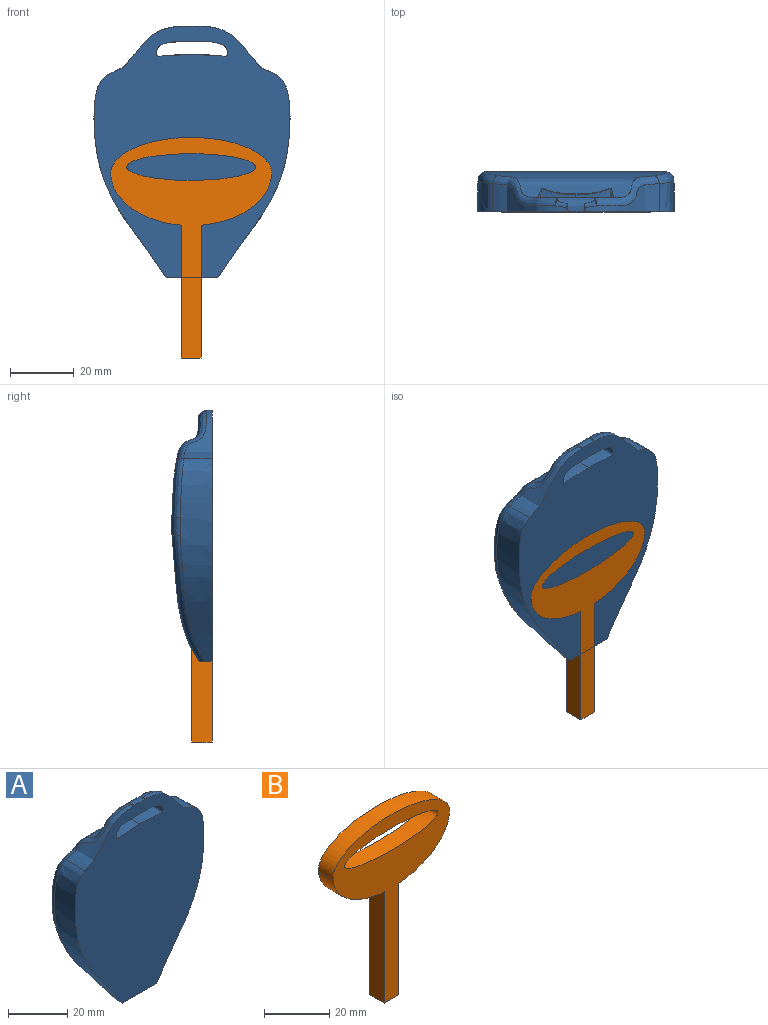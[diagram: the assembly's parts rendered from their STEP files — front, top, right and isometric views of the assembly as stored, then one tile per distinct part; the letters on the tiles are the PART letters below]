
ASSEMBLY  parts=2 mates=1
PART A: 34 faces, bbox 62.2x13.4x80.2 mm
  f0: bspline ~1.98x0.93mm, area 0.2mm2, adj f9,f10,f11
  f1: extruded ~54.94x39.8mm, area 1494.4mm2, adj f3,f4,f5,f6,f7,f13
  f2: bspline ~1.98x0.93mm, area 0.2mm2, adj f15,f16,f17
  f3: bspline ~10.82x3.82mm, area 23.1mm2, adj f1,f4,f13,f14,f27
  f4: bspline ~43.26x24.45mm, area 173.7mm2, adj f1,f3,f5,f26,f27
  f5: plane 15.96x1.26mm, normal (0,0.02,-1), area 12.5mm2, adj f1,f4,f6,f26
  f6: bspline ~43.26x24.45mm, area 173.8mm2, adj f1,f5,f7,f25,f26
  f7: bspline ~11.83x4.04mm, area 23.1mm2, adj f1,f6,f12,f13,f25
  f8: bspline ~1.1x0.26mm, area 0.1mm2, adj f9,f21,f24
  f9: bspline ~4.26x2.61mm, area 5.6mm2, adj f0,f8,f21,f24,f29
  f10: bspline ~1.25x0.54mm, area 0.1mm2, adj f0,f11,f24
  f11: bspline ~20.97x16.97mm, area 94.1mm2, adj f0,f10,f12,f24,f29
  f12: bspline ~19.64x6.21mm, area 75.1mm2, adj f7,f11,f13,f24,f25,f29
  f13: plane 56.13x5.66mm, normal (0,1,0), area 314.2mm2, adj f1,f3,f7,f12,f14,f24
  f14: bspline ~19.61x6.15mm, area 75.1mm2, adj f3,f13,f15,f24,f27,f28
  f15: bspline ~20.97x16.97mm, area 94.1mm2, adj f2,f14,f16,f24,f28
  f16: bspline ~1.25x0.54mm, area 0.1mm2, adj f2,f15,f24
  f17: bspline ~4.01x2.57mm, area 5.6mm2, adj f2,f18,f20,f24,f28
  f18: bspline ~1.1x0.27mm, area 0.1mm2, adj f17,f20,f24
  f19: bspline ~18.08x5.39mm, area 14.5mm2, adj f24,f30,f32
  f20: bspline ~0.22x0.19mm, area 0mm2, adj f17,f18,f22
  f21: bspline ~0.22x0.19mm, area 0mm2, adj f8,f9,f23
  f22: bspline ~1.69x0.72mm, area 0.3mm2, adj f20,f24,f28,f33
  f23: bspline ~1.69x0.72mm, area 0.3mm2, adj f21,f24,f29,f33
  f24: extruded ~56.41x33.39mm, area 1410.5mm2, adj f8,f9,f10,f11,f12,f13,f14,f15
  f25: extruded ~63.73x22.62mm, area 596.7mm2, adj f6,f7,f12,f26,f29,f33
  f26: plane 16.35x3.32mm, normal (0,0,-1), area 52.1mm2, adj f4,f5,f6,f25,f27,f33
  f27: extruded ~63.73x22.62mm, area 596.7mm2, adj f3,f4,f14,f26,f28,f33
  f28: extruded ~23.59x15.13mm, area 115.1mm2, adj f14,f15,f17,f22,f27,f33
  f29: extruded ~23.59x15.13mm, area 115.1mm2, adj f9,f11,f12,f23,f25,f33
  f30: bspline ~18.08x5.39mm, area 14.5mm2, adj f19,f24,f31
  f31: extruded ~11.21x7.24mm, area 119.8mm2, adj f30,f32,f33
  f32: extruded ~11.21x7.24mm, area 119.8mm2, adj f19,f31,f33
  f33: plane 78.9x61.81mm, normal (0,-1,0), area 3529.4mm2, adj f22,f23,f24,f25,f26,f27,f28,f29
PART B: 9 faces, bbox 50.5x6.4x69.2 mm
  f0: plane 41.66x6.35mm, normal (1,0,0), area 264.6mm2, adj f1,f6,f7,f8
  f1: extruded ~22.08x15.45mm, area 184.9mm2, adj f0,f2,f7,f8
  f2: extruded ~50.46x12.08mm, area 388mm2, adj f1,f3,f7,f8
  f3: extruded ~22.08x15.45mm, area 184.9mm2, adj f2,f4,f7,f8
  f4: plane 41.66x6.35mm, normal (-1,0,0), area 264.6mm2, adj f3,f6,f7,f8
  f5: extruded ~40.38x8.43mm, area 541.2mm2, adj f7,f8
  f6: plane 6.35x6.19mm, normal (0,0,-1), area 39.3mm2, adj f0,f4,f7,f8
  f7: plane 69.19x50.48mm, normal (0,-1,0), area 1085.7mm2, adj f0,f1,f2,f3,f4,f5,f6
  f8: plane 69.19x50.48mm, normal (0,1,0), area 1085.7mm2, adj f0,f1,f2,f3,f4,f5,f6
PLACE A t=(-2.97,5.31,3.82)mm fixed
PLACE B t=(-4.75,-0.93,-3.33)mm
MATE planar B.f7 <-> A.f33  axis (0,-1,0) through (-4.75,-7.28,-14.82)mm
